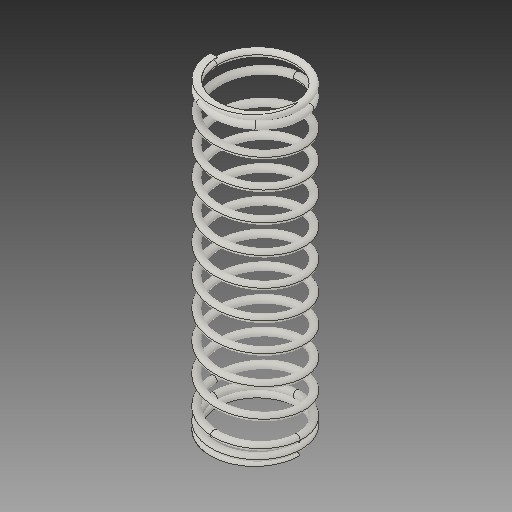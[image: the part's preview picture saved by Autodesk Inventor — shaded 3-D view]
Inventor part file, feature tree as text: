
AUTODESK INVENTOR PART (.ipt)
format: ipt  version: 2019 (Build 230136000, 136)  size: 946,688 bytes
history: native  units: in
note: dims shown in document units (in); Inventor stores cm internally (conversion verified against a paired STEP export)
features: other x59, helix x2, plane x1
ambient origin geometry x8: Origin, YZ Plane, XZ Plane, XY Plane, X Axis, Y Axis, Z Axis, Center Point
bodies: Solid1 (feature_tree)
feature tree (62):
  other  "Compress Spring1"
  other  "Solid1::Compress Spring1"
  other  "TaggingFeature1"
  other  "Path Section Sketch(Right)"
  helix  "Coil Section Sketch(Right)"  [1 undecoded]
  other  "Start Transition Coil Sketch 1(Right)"
  other  "Start Transition Coil Sketch 2(Right)"
  other  "Start Transition Coil Sketch 3(Right)"
  other  "Start Transition Coil Sketch 4(Right)"
  other  "Start Ends Skecth(Right)"
  other  "Start Cut Sketch(Right)"
  other  "End Transition Coil Sketch 1(Right)"
  other  "End Transition Coil Sketch 2(Right)"
  other  "End Transition Coil Sketch 3(Right)"
  other  "End Transition Coil Sketch 4(Right)"
  other  "End Coil Skecth(Right)"
  other  "End Cut Sketch(Right)"
  other  "Plain Ends Cut Sketch 1(Right)"
  other  "Plain Ends Cut Sketch 2(Right)"
  other  "Path Section Sketch(Left)"
  helix  "Coil Section Sketch(Left)"  [1 undecoded]
  other  "Start Transition Coil Sketch 1(Left)"
  other  "Start Transition Coil Sketch 2(Left)"
  other  "Start Transition Coil Sketch 3(Left)"
  other  "Start Transition Coil Sketch 4(Left)"
  other  "Start Ends Skecth(Left)"
  other  "Start Cut Sketch(Left)"
  other  "End Transition Coil Sketch 1(Left)"
  other  "End Transition Coil Sketch 2(Left)"
  other  "End Transition Coil Sketch 3(Left)"
  other  "End Transition Coil Sketch 4(Left)"
  other  "End Coil Skecth(Left)"
  other  "End Cut Sketch(Left)"
  other  "Plain Ends Cut Sketch 1(Left)"
  other  "Plain Ends Cut Sketch 2(Left)"
  other  "Main Coil Path(Right)"
  other  "Main Coil Path(Left)"
  other  "Section Work Plane(Right)"
  other  "Start Work Plane(Right)"
  other  "End Work Plane(Right)"
  other  "End Cut Work Plane(Right)"
  other  "Start Cut Work Plane(Right)"
  other  "Plain Ends Cut Work Plane 1(Right)"
  other  "Plain Ends Cut Work Plane 2(Right)"
  other  "Section Work Plane(Left)"
  other  "Start Work Plane(Left)"
  other  "End Work Plane(Left)"
  other  "End Cut Work Plane(Left)"
  other  "Start Cut Work Plane(Left)"
  other  "Plain Ends Cut Work Plane 2(Left)"
  other  "Plain Ends Cut Work Plane 1(Left)"
  other  "iMate Based Work Plane"
  plane  "Work Plane Start Section"
  other  "Y Axis_1"
  other  "Preview X Axis"
  other  "Preview Center Point"
  other  "Srf1"
  other  "Srf2"
  other  "Srf1::Derived"
  other  "Srf2::Derived"
  other  "Axial"
  other  "Planar"
note: 2 required parameter values undecoded (feature->parameter linkage not recoverable at this tier; creation-order binding heuristic only, values carry confidence <= 0.55)
